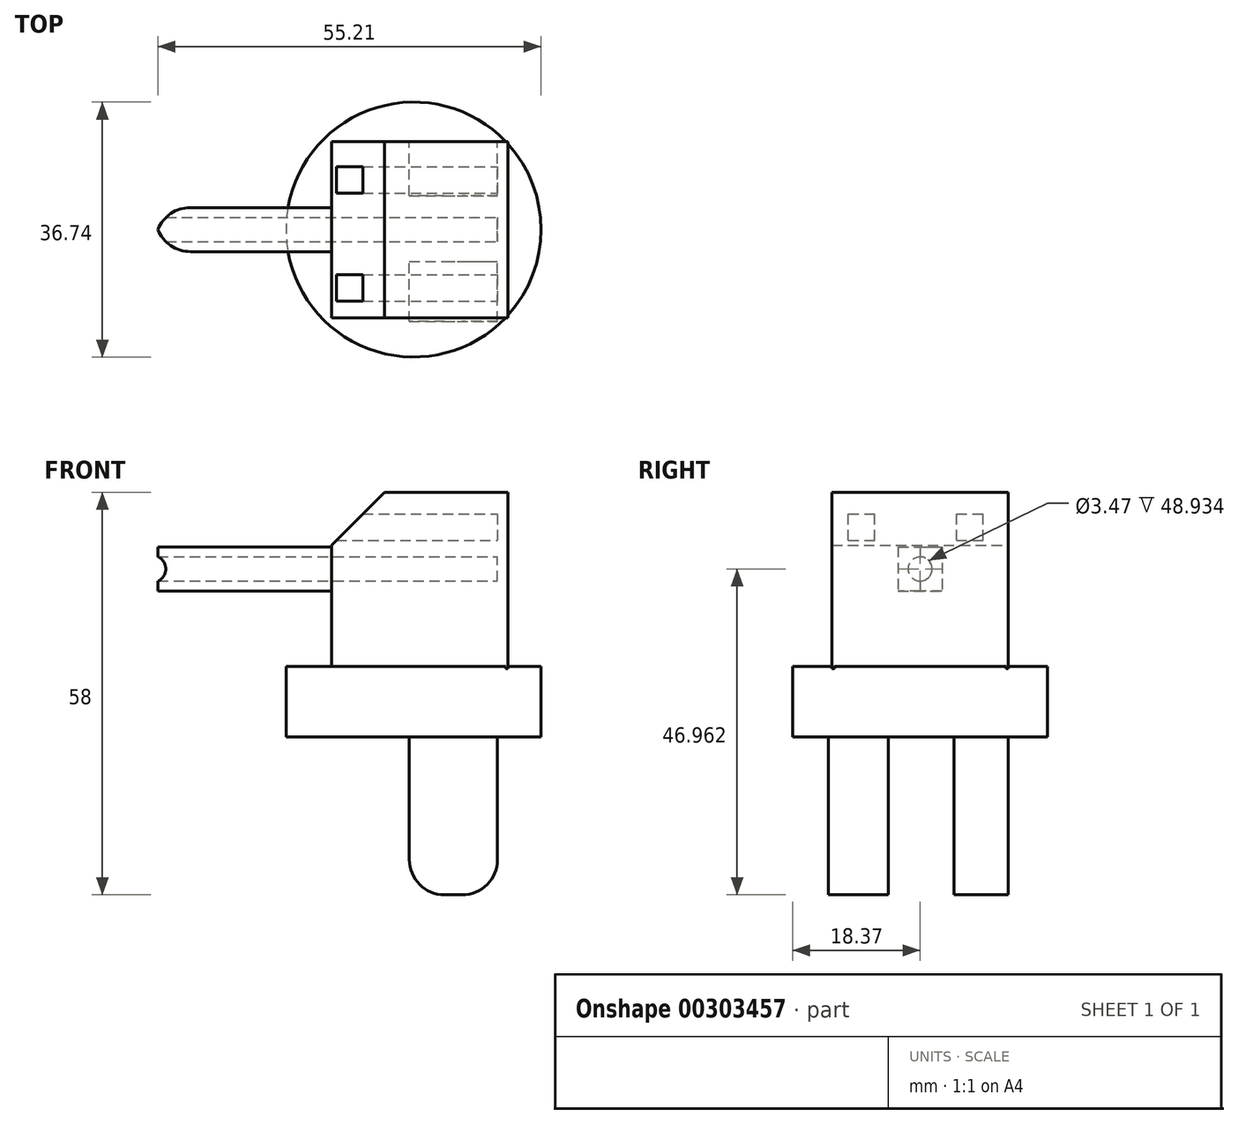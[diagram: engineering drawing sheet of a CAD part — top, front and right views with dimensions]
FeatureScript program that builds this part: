
annotation { "Feature Type Name" : "Feature", "Feature Type Description" : "" }
export const myFeature = defineFeature(function(context is Context, id is Id, definition is map)
    precondition{}
    {
        {
            var Q0;
            Q0=qCreatedBy(makeId("Front.planeOp"),FACE);
            var sketch = newSketch(context, id + "F0", { "sketchPlane" : qUnion([Q0])});
            skLineSegment(sketch, "E0.bottom", {"start": v(-23.9, 35.26) * mm, "end": v(1.5, 35.26) * mm});
            skLineSegment(sketch, "E0.top", {"start": v(-23.9, 9.86) * mm, "end": v(1.5, 9.86) * mm});
            skLineSegment(sketch, "E0.left", {"start": v(-23.9, 35.26) * mm, "end": v(-23.9, 9.86) * mm});
            skLineSegment(sketch, "E0.right", {"start": v(1.5, 35.26) * mm, "end": v(1.5, 9.86) * mm});
            skLineSegment(sketch, "E1", {"start": v(-23.9, 27.4) * mm, "end": v(-49.3, 27.4) * mm});
            skLineSegment(sketch, "E2", {"start": v(-49.3, 27.4) * mm, "end": v(-49.3, 21.05) * mm});
            skLineSegment(sketch, "E3", {"start": v(-49.3, 21.05) * mm, "end": v(-23.9, 21.05) * mm});
            skSolve(sketch);
        }
        {
            var Q0;
            {var subQ3=sQuery(id+"F0.wireOp",EDGE,"E0.bottom");Q0=makeQuery(id+"F0.imprint","IMPRINT",FACE,{"disambiguationData":[TD([[makeQuery(id+"F0.imprint","IMPRINT",EDGE,{"derivedFrom":subQ3}),-1.0]])]});}
            extrude(context, id + "F1", {"entities" : qUnion([Q0]), "endBound" : BoundingType.SYMMETRIC, "depth" : 25.4 * mm});
        }
        {
            var Q0;
            {var subQ0=sQuery(id+"F0.wireOp",EDGE,"E1");Q0=makeQuery(id+"F0.imprint","IMPRINT",FACE,{"disambiguationData":[TD([[makeQuery(id+"F0.imprint","IMPRINT",EDGE,{"derivedFrom":subQ0}),1.0]])]});}
            extrude(context, id + "F2", {"entities" : qUnion([Q0]), "operationType" : NewBodyOperationType.ADD, "endBound" : BoundingType.SYMMETRIC, "depth" : 6.35 * mm});
        }
        {
            var Q0;
            Q0=makeQuery(id+"F1.opExtrude","SWEPT_EDGE",EDGE,{"disambiguationData":[OSD([sQuery(id+"F0.wireOp",EDGE,"E0.bottom"),sQuery(id+"F0.wireOp",EDGE,"E0.left")])]});
            chamfer(context, id + "F3", {"entities" : qUnion([Q0]), "width" : 7.62 * mm, "tangentPropagation" : true});
        }
        {
            var Q0;
            Q0=qCreatedBy(makeId("Top.planeOp"),FACE);
            var sketch = newSketch(context, id + "F4", { "sketchPlane" : qUnion([Q0])});
            skCircle(sketch, "E4", {"center": v(-12.09, 0) * mm, "radius": 18.37 * mm});
            skSolve(sketch);
        }
        {
            var Q0;
            Q0 = qSketchRegion(id + "F4", true);
            extrude(context, id + "F5", {"entities" : qUnion([Q0]), "operationType" : NewBodyOperationType.ADD, "depth" : 10.16 * mm});
        }
        {
            var Q0;
            Q0=qCreatedBy(makeId("Right.planeOp"),FACE);
            var sketch = newSketch(context, id + "F6", { "sketchPlane" : qUnion([Q0])});
            skLineSegment(sketch, "E5", {"start": v(12.66, 0) * mm, "end": v(12.66, -22.74) * mm});
            skLineSegment(sketch, "E6", {"start": v(12.66, -22.74) * mm, "end": v(4.9, -22.74) * mm});
            skLineSegment(sketch, "E7", {"start": v(4.9, -22.74) * mm, "end": v(4.9, 0) * mm});
            skLineSegment(sketch, "E8", {"start": v(4.9, 0) * mm, "end": v(-4.6, 0) * mm});
            skLineSegment(sketch, "E9", {"start": v(-4.6, 0) * mm, "end": v(-4.6, -22.74) * mm});
            skLineSegment(sketch, "E10", {"start": v(-4.6, -22.74) * mm, "end": v(-13.24, -22.74) * mm});
            skLineSegment(sketch, "E11", {"start": v(-13.24, -22.74) * mm, "end": v(-13.24, 0) * mm});
            skLineSegment(sketch, "E12", {"start": v(-13.24, 0) * mm, "end": v(12.66, 0) * mm});
            skSolve(sketch);
        }
        {
            var Q0;
            Q0 = qSketchRegion(id + "F6", true);
            extrude(context, id + "F7", {"entities" : qUnion([Q0]), "operationType" : NewBodyOperationType.ADD, "oppositeDirection" : true, "depth" : 12.7 * mm});
        }
        {
            var Q0;
            Q0=makeQuery(id+"F7.opExtrude","CAP_EDGE",EDGE,{"disambiguationData":[OSD([sQuery(id+"F6.wireOp",EDGE,"E6")])],"isStart":false});
            var Q1;
            Q1=makeQuery(id+"F7.opExtrude","CAP_EDGE",EDGE,{"disambiguationData":[OSD([sQuery(id+"F6.wireOp",EDGE,"E10")])],"isStart":false});
            var Q2;
            Q2=makeQuery(id+"F7.opExtrude","CAP_EDGE",EDGE,{"disambiguationData":[OSD([sQuery(id+"F6.wireOp",EDGE,"E10")])],"isStart":true});
            var Q3;
            Q3=makeQuery(id+"F7.opExtrude","CAP_EDGE",EDGE,{"disambiguationData":[OSD([sQuery(id+"F6.wireOp",EDGE,"E6")])],"isStart":true});
            fillet(context, id + "F8", {"entities" : qUnion([Q0, Q1, Q2, Q3]), "radius" : 5.08 * mm, "tangentPropagation" : true, "allowEdgeOverflow" : false});
        }
        {
            var Q0;
            Q0=qCreatedBy(makeId("Right.planeOp"),FACE);
            var sketch = newSketch(context, id + "F9", { "sketchPlane" : qUnion([Q0])});
            skCircle(sketch, "E13", {"center": v(0, 24.22) * mm, "radius": 1.74 * mm});
            skSolve(sketch);
        }
        {
            var Q0;
            Q0 = qSketchRegion(id + "F9", true);
            extrude(context, id + "F10", {"entities" : qUnion([Q0]), "operationType" : NewBodyOperationType.REMOVE, "oppositeDirection" : true, "depth" : 177.8 * mm});
        }
        {
            var Q0;
            Q0=makeQuery(id+"F2.opExtrude","CAP_EDGE",EDGE,{"disambiguationData":[OSD([sQuery(id+"F0.wireOp",EDGE,"E2")])],"isStart":true});
            var Q1;
            Q1=makeQuery(id+"F2.opExtrude","CAP_EDGE",EDGE,{"disambiguationData":[OSD([sQuery(id+"F0.wireOp",EDGE,"E2")])],"isStart":false});
            fillet(context, id + "F11", {"entities" : qUnion([Q0, Q1]), "radius" : 5.08 * mm, "tangentPropagation" : true, "allowEdgeOverflow" : false});
        }
        {
            var Q0;
            Q0=qCreatedBy(makeId("Right.planeOp"),FACE);
            var sketch = newSketch(context, id + "F12", { "sketchPlane" : qUnion([Q0])});
            skLineSegment(sketch, "E14.bottom", {"start": v(9.05, 32.14) * mm, "end": v(5.24, 32.14) * mm});
            skLineSegment(sketch, "E14.top", {"start": v(9.05, 28.33) * mm, "end": v(5.24, 28.33) * mm});
            skLineSegment(sketch, "E14.left", {"start": v(9.05, 32.14) * mm, "end": v(9.05, 28.33) * mm});
            skLineSegment(sketch, "E14.right", {"start": v(5.24, 32.14) * mm, "end": v(5.24, 28.33) * mm});
            skLineSegment(sketch, "E15.bottom", {"start": v(-6.53, 32.14) * mm, "end": v(-10.34, 32.14) * mm});
            skLineSegment(sketch, "E15.top", {"start": v(-6.53, 28.33) * mm, "end": v(-10.34, 28.33) * mm});
            skLineSegment(sketch, "E15.left", {"start": v(-6.53, 32.14) * mm, "end": v(-6.53, 28.33) * mm});
            skLineSegment(sketch, "E15.right", {"start": v(-10.34, 32.14) * mm, "end": v(-10.34, 28.33) * mm});
            skSolve(sketch);
        }
        {
            var Q0;
            Q0 = qSketchRegion(id + "F12", true);
            extrude(context, id + "F13", {"entities" : qUnion([Q0]), "operationType" : NewBodyOperationType.REMOVE, "oppositeDirection" : true, "depth" : 25.4 * mm});
        }
    });
